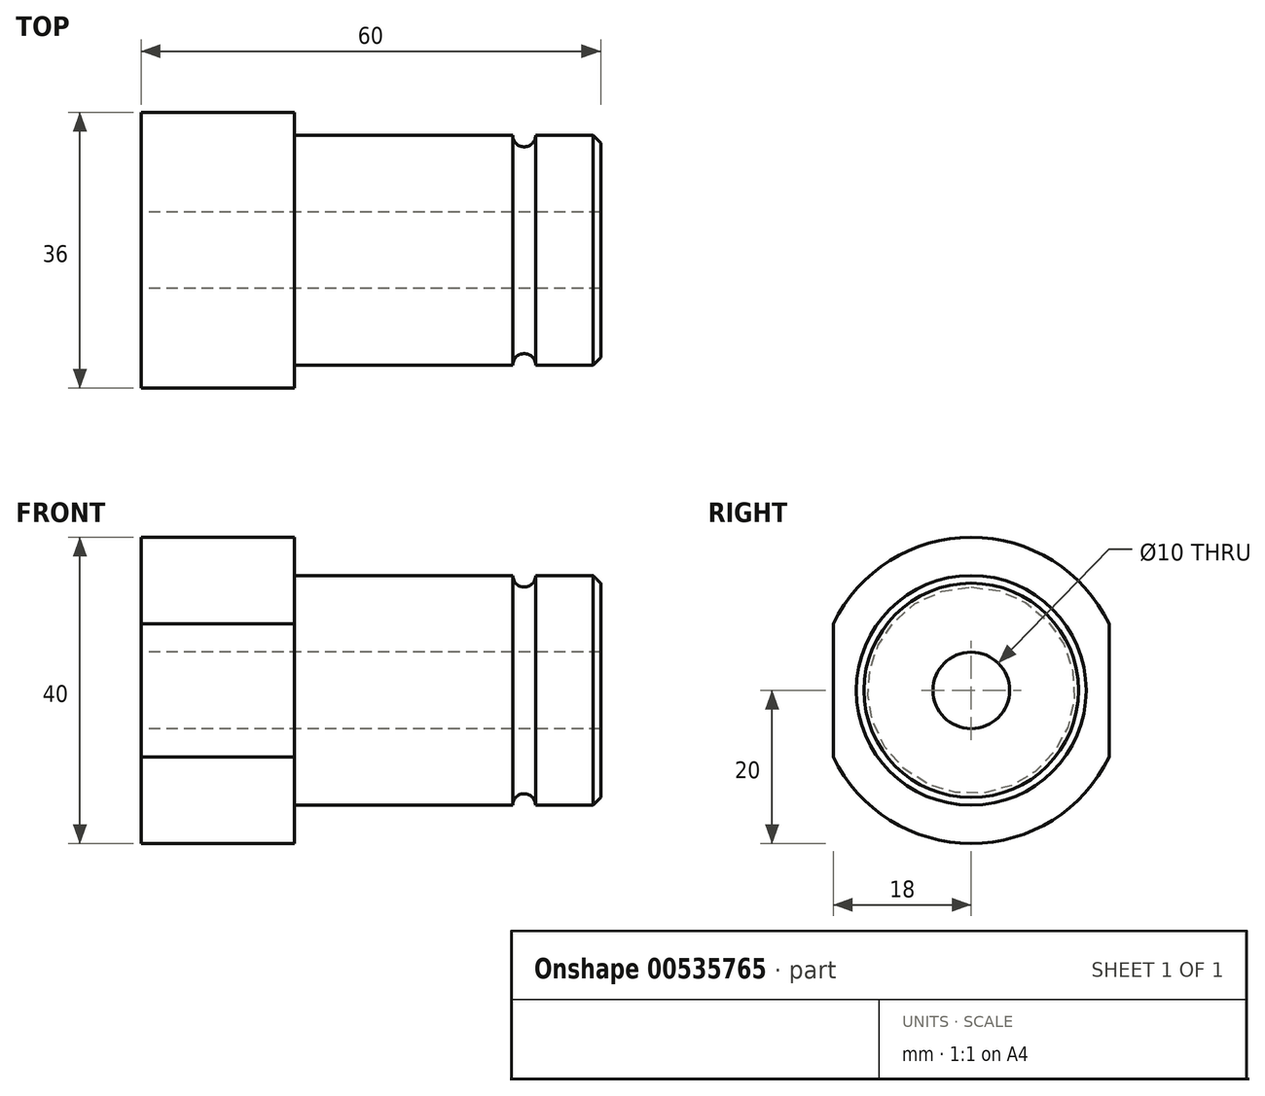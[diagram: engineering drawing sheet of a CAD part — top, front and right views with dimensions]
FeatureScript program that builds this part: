
annotation { "Feature Type Name" : "Feature", "Feature Type Description" : "" }
export const myFeature = defineFeature(function(context is Context, id is Id, definition is map)
    precondition{}
    {
        {
            var Q0;
            Q0=qCreatedBy(makeId("Front.planeOp"),FACE);
            var sketch = newSketch(context, id + "F0", { "sketchPlane" : qUnion([Q0])});
            skLineSegment(sketch, "E0", {"start": v(-79.49, 0) * mm, "end": v(11.39, 0) * mm, "construction": true});
            skLineSegment(sketch, "E1", {"start": v(0, 0) * mm, "end": v(0, 15) * mm});
            skLineSegment(sketch, "E2", {"start": v(0, 15) * mm, "end": v(-40, 15) * mm});
            skLineSegment(sketch, "E3", {"start": v(-40, 15) * mm, "end": v(-40, 20) * mm});
            skLineSegment(sketch, "E4", {"start": v(-40, 20) * mm, "end": v(-60, 20) * mm});
            skLineSegment(sketch, "E5", {"start": v(-60, 20) * mm, "end": v(-60, 0) * mm});
            skLineSegment(sketch, "E6", {"start": v(-60, 0) * mm, "end": v(0, 0) * mm});
            skPoint(sketch, "E7", {"position": v(-10, 15) * mm});
            skCircle(sketch, "E8", {"center": v(-10, 15) * mm, "radius": 1.5 * mm});
            skSolve(sketch);
        }
        {
            var Q0;
            Q0=makeQuery(id+"F0.imprint","IMPRINT",FACE,{"disambiguationData":[TD([[makeQuery(id+"F0.imprint","IMPRINT",EDGE,{"derivedFrom":sQuery(id+"F0.wireOp",EDGE,"E1")}),1.0]])]});
            var Q1;
            Q1=sQuery(id+"F0.wireOp",EDGE,"E0");
            revolve(context, id + "F1", {"entities" : qUnion([Q0]), "axis" : qUnion([Q1]), "revolveType" : RevolveType.FULL});
        }
        {
            var Q0;
            Q0=makeQuery(id+"F1.opRevolve","SWEPT_FACE",FACE,{"disambiguationData":[OSD([sQuery(id+"F0.wireOp",EDGE,"E5")])]});
            var sketch = newSketch(context, id + "F2", { "sketchPlane" : qUnion([Q0])});
            skCircle(sketch, "E9", {"center": v(0, 0) * mm, "radius": 5 * mm});
            skSolve(sketch);
        }
        {
            var Q0;
            Q0=makeQuery(id+"F2.imprint","IMPRINT",FACE,{"disambiguationData":[TD([[makeQuery(id+"F2.imprint","IMPRINT",EDGE,{"derivedFrom":sQuery(id+"F2.wireOp",EDGE,"E9")}),1.0]])]});
            var Q1;
            Q1=sQuery(id+"F2.wireOp",EDGE,"E9");
            extrude(context, id + "F3", {"entities" : qUnion([Q0]), "operationType" : NewBodyOperationType.REMOVE, "surfaceEntities" : qUnion([Q1]), "endBound" : BoundingType.UP_TO_NEXT, "oppositeDirection" : true, "depth" : 25 * mm, "offsetDistance" : 25 * mm});
        }
        {
            var Q0;
            Q0=makeQuery(id+"F1.opRevolve","SWEPT_EDGE",EDGE,{"disambiguationData":[OSD([sQuery(id+"F0.wireOp",EDGE,"E1"),sQuery(id+"F0.wireOp",EDGE,"E2")])]});
            chamfer(context, id + "F4", {"entities" : qUnion([Q0]), "width" : 1 * mm, "tangentPropagation" : true});
        }
        {
            var Q0;
            Q0=makeQuery(id+"F1.opRevolve","SWEPT_FACE",FACE,{"disambiguationData":[OSD([sQuery(id+"F0.wireOp",EDGE,"E5")])]});
            var sketch = newSketch(context, id + "F5", { "sketchPlane" : qUnion([Q0])});
            skLineSegment(sketch, "E10", {"start": v(-18, 8.72) * mm, "end": v(-18, -8.72) * mm});
            skLineSegment(sketch, "E11", {"start": v(18, 8.72) * mm, "end": v(18, -8.72) * mm});
            skSolve(sketch);
        }
        {
            var Q0;
            {var subQ0=sQuery(id+"F5.wireOp",EDGE,"E10");Q0=makeQuery(id+"F5.imprint","IMPRINT",FACE,{"disambiguationData":[TD([[makeQuery(id+"F5.imprint","IMPRINT",EDGE,{"derivedFrom":subQ0}),-1.0]])]});}
            extrude(context, id + "F6", {"entities" : qUnion([Q0]), "operationType" : NewBodyOperationType.REMOVE, "endBound" : BoundingType.UP_TO_NEXT, "oppositeDirection" : true, "depth" : 25 * mm, "offsetDistance" : 25 * mm});
        }
        {
            var Q0;
            {var subQ0=sQuery(id+"F5.wireOp",EDGE,"E11");Q0=makeQuery(id+"F5.imprint","IMPRINT",FACE,{"disambiguationData":[TD([[makeQuery(id+"F5.imprint","IMPRINT",EDGE,{"derivedFrom":subQ0}),1.0]])]});}
            extrude(context, id + "F7", {"entities" : qUnion([Q0]), "operationType" : NewBodyOperationType.REMOVE, "oppositeDirection" : true, "depth" : 25 * mm, "offsetDistance" : 25 * mm});
        }
    });
